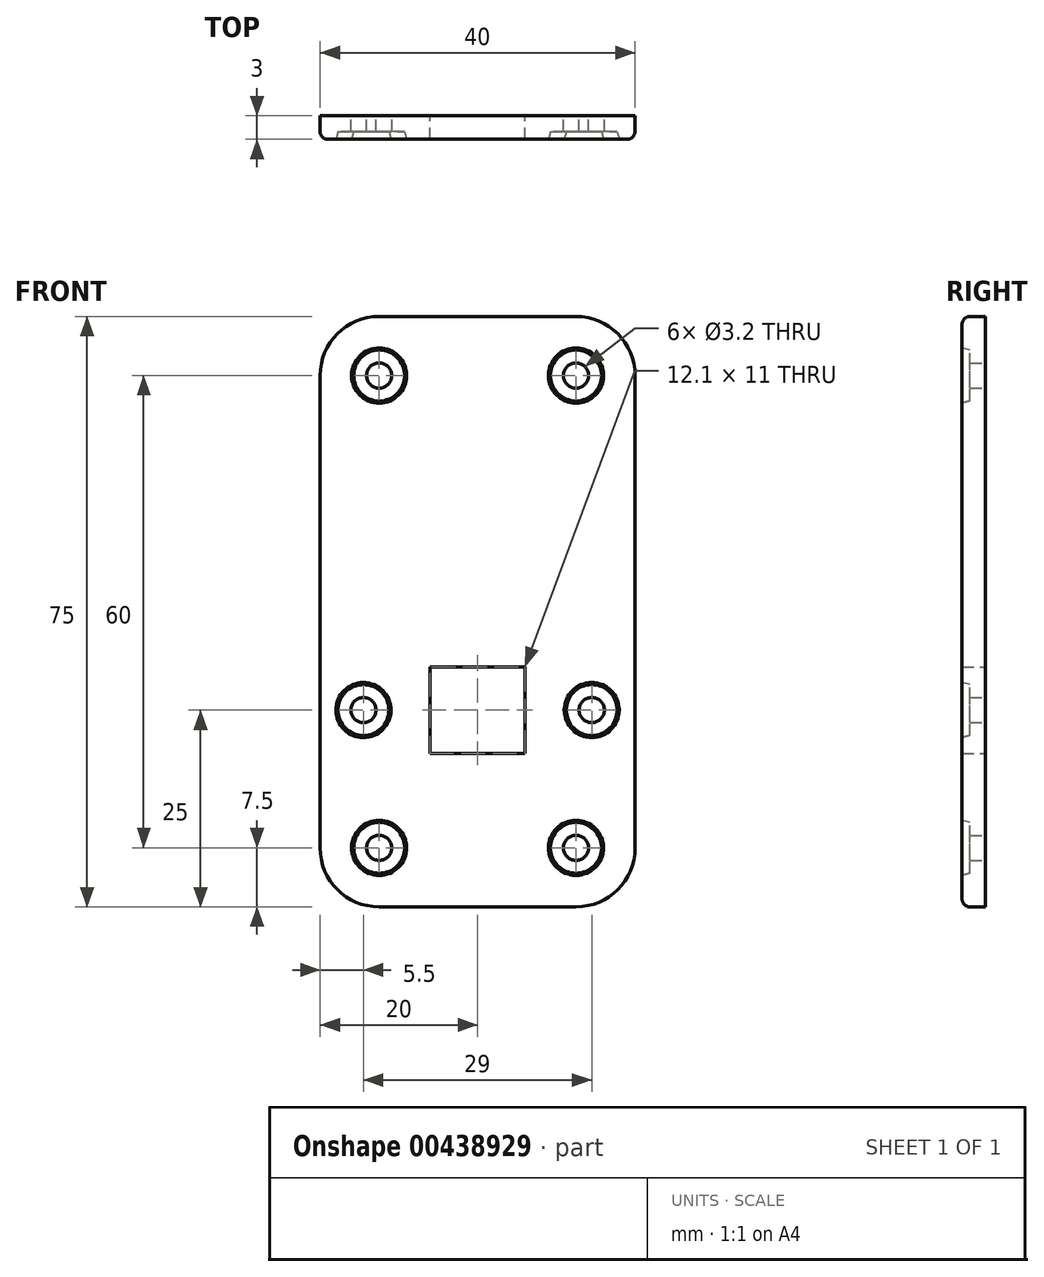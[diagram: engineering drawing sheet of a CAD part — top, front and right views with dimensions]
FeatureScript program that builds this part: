
annotation { "Feature Type Name" : "Feature", "Feature Type Description" : "" }
export const myFeature = defineFeature(function(context is Context, id is Id, definition is map)
    precondition{}
    {
        {
            var Q0;
            Q0=qCreatedBy(makeId("Front.planeOp"),FACE);
            var sketch = newSketch(context, id + "F0", { "sketchPlane" : qUnion([Q0])});
            skLineSegment(sketch, "E0.bottom", {"start": v(0, 75) * mm, "end": v(40, 75) * mm});
            skLineSegment(sketch, "E0.top", {"start": v(0, 0) * mm, "end": v(40, 0) * mm});
            skLineSegment(sketch, "E0.left", {"start": v(0, 75) * mm, "end": v(0, 0) * mm});
            skLineSegment(sketch, "E0.right", {"start": v(40, 75) * mm, "end": v(40, 0) * mm});
            skLineSegment(sketch, "E1.bottom", {"start": v(13.95, 30.5) * mm, "end": v(26.05, 30.5) * mm});
            skLineSegment(sketch, "E1.top", {"start": v(13.95, 19.5) * mm, "end": v(26.05, 19.5) * mm});
            skLineSegment(sketch, "E1.left", {"start": v(13.95, 30.5) * mm, "end": v(13.95, 19.5) * mm});
            skLineSegment(sketch, "E1.right", {"start": v(26.05, 30.5) * mm, "end": v(26.05, 19.5) * mm});
            skCircle(sketch, "E2", {"center": v(5.5, 25) * mm, "radius": 1.6 * mm});
            skCircle(sketch, "E3", {"center": v(34.5, 25) * mm, "radius": 1.6 * mm});
            skCircle(sketch, "E4", {"center": v(7.5, 67.5) * mm, "radius": 1.6 * mm});
            skCircle(sketch, "E5", {"center": v(32.5, 67.5) * mm, "radius": 1.6 * mm});
            skCircle(sketch, "E6", {"center": v(7.5, 7.5) * mm, "radius": 1.6 * mm});
            skCircle(sketch, "E7", {"center": v(32.5, 7.5) * mm, "radius": 1.6 * mm});
            skLineSegment(sketch, "E8", {"start": v(5.5, 25) * mm, "end": v(34.5, 25) * mm, "construction": true});
            skPoint(sketch, "E9.endSnap0", {"position": v(20, 25) * mm});
            skPoint(sketch, "E10.endSnap0", {"position": v(20, 19.5) * mm});
            skLineSegment(sketch, "E11", {"start": v(20, 30.5) * mm, "end": v(20, 25) * mm, "construction": true});
            skLineSegment(sketch, "E12", {"start": v(20, 19.5) * mm, "end": v(20, 25) * mm, "construction": true});
            skLineSegment(sketch, "E13", {"start": v(0, 15) * mm, "end": v(40, 15) * mm, "construction": true});
            skLineSegment(sketch, "E14", {"start": v(0, 60) * mm, "end": v(40, 60) * mm, "construction": true});
            skLineSegment(sketch, "E15", {"start": v(8.25, 25) * mm, "end": v(31.75, 25) * mm, "construction": true});
            skArc(sketch, "E16.0.startCap", {"start": v(8.25, 17.5) * mm, "mid": v(0.75, 25) * mm, "end": v(8.25, 32.5) * mm, "construction": true});
            skArc(sketch, "E16.0.endCap", {"start": v(31.75, 32.5) * mm, "mid": v(39.25, 25) * mm, "end": v(31.75, 17.5) * mm, "construction": true});
            skLineSegment(sketch, "E16.0.left", {"start": v(8.25, 32.5) * mm, "end": v(31.75, 32.5) * mm, "construction": true});
            skLineSegment(sketch, "E16.0.right", {"start": v(8.25, 17.5) * mm, "end": v(31.75, 17.5) * mm, "construction": true});
            skLineSegment(sketch, "E17", {"start": v(20, 75) * mm, "end": v(20, 25) * mm, "construction": true});
            skSolve(sketch);
        }
        {
            var Q0;
            Q0=makeQuery(id+"F0.imprint","IMPRINT",FACE,{"disambiguationData":[TD([[makeQuery(id+"F0.imprint","IMPRINT",EDGE,{"derivedFrom":sQuery(id+"F0.wireOp",EDGE,"E0.bottom")}),-1.0]])]});
            extrude(context, id + "F1", {"entities" : qUnion([Q0]), "depth" : 3 * mm});
        }
        {
            var Q0;
            Q0=makeQuery(id+"F1.opExtrude","SWEPT_EDGE",EDGE,{"disambiguationData":[OSD([sQuery(id+"F0.wireOp",EDGE,"E0.bottom"),sQuery(id+"F0.wireOp",EDGE,"E0.right")])]});
            var Q1;
            Q1=makeQuery(id+"F1.opExtrude","SWEPT_EDGE",EDGE,{"disambiguationData":[OSD([sQuery(id+"F0.wireOp",EDGE,"E0.top"),sQuery(id+"F0.wireOp",EDGE,"E0.right")])]});
            var Q2;
            Q2=makeQuery(id+"F1.opExtrude","SWEPT_EDGE",EDGE,{"disambiguationData":[OSD([sQuery(id+"F0.wireOp",EDGE,"E0.top"),sQuery(id+"F0.wireOp",EDGE,"E0.left")])]});
            var Q3;
            Q3=makeQuery(id+"F1.opExtrude","SWEPT_EDGE",EDGE,{"disambiguationData":[OSD([sQuery(id+"F0.wireOp",EDGE,"E0.bottom"),sQuery(id+"F0.wireOp",EDGE,"E0.left")])]});
            fillet(context, id + "F2", {"entities" : qUnion([Q0, Q1, Q2, Q3]), "radius" : 7.5 * mm, "tangentPropagation" : true, "allowEdgeOverflow" : false});
        }
        {
            var Q0;
            Q0=makeQuery(id+"F1.opExtrude","CAP_FACE",FACE,{"disambiguationData":[OSD([sQuery(id+"F0.wireOp",EDGE,"E0.bottom"),sQuery(id+"F0.wireOp",EDGE,"E0.top"),sQuery(id+"F0.wireOp",EDGE,"E0.left"),sQuery(id+"F0.wireOp",EDGE,"E0.right"),sQuery(id+"F0.wireOp",EDGE,"E1.bottom"),sQuery(id+"F0.wireOp",EDGE,"E1.top"),sQuery(id+"F0.wireOp",EDGE,"E1.left"),sQuery(id+"F0.wireOp",EDGE,"E1.right"),sQuery(id+"F0.wireOp",EDGE,"E2"),sQuery(id+"F0.wireOp",EDGE,"E3"),sQuery(id+"F0.wireOp",EDGE,"E4"),sQuery(id+"F0.wireOp",EDGE,"E5"),sQuery(id+"F0.wireOp",EDGE,"E6"),sQuery(id+"F0.wireOp",EDGE,"E7")])],"isStart":false});
            var sketch = newSketch(context, id + "F3", { "sketchPlane" : qUnion([Q0])});
            skCircle(sketch, "E18", {"center": v(7.5, 67.5) * mm, "radius": 3.5 * mm});
            skCircle(sketch, "E19", {"center": v(32.5, 67.5) * mm, "radius": 3.5 * mm});
            skCircle(sketch, "E20", {"center": v(5.5, 25) * mm, "radius": 3.5 * mm});
            skCircle(sketch, "E21", {"center": v(32.5, 7.5) * mm, "radius": 3.5 * mm});
            skCircle(sketch, "E22", {"center": v(7.5, 7.5) * mm, "radius": 3.5 * mm});
            skCircle(sketch, "E23", {"center": v(34.5, 25) * mm, "radius": 3.5 * mm});
            skSolve(sketch);
        }
        {
            var Q0;
            Q0 = qSketchRegion(id + "F3", true);
            extrude(context, id + "F4", {"entities" : qUnion([Q0]), "operationType" : NewBodyOperationType.REMOVE, "oppositeDirection" : true, "depth" : 1 * mm, "hasDraft" : true, "draftAngle" : 15 * degree, "draftPullDirection" : true});
        }
        {
            var Q0;
            Q0=makeQuery(id+"F1.opExtrude","CAP_EDGE",EDGE,{"disambiguationData":[OSD([sQuery(id+"F0.wireOp",EDGE,"E0.top")])],"isStart":false});
            fillet(context, id + "F5", {"entities" : qUnion([Q0]), "radius" : 1 * mm, "tangentPropagation" : true, "allowEdgeOverflow" : false});
        }
    });
